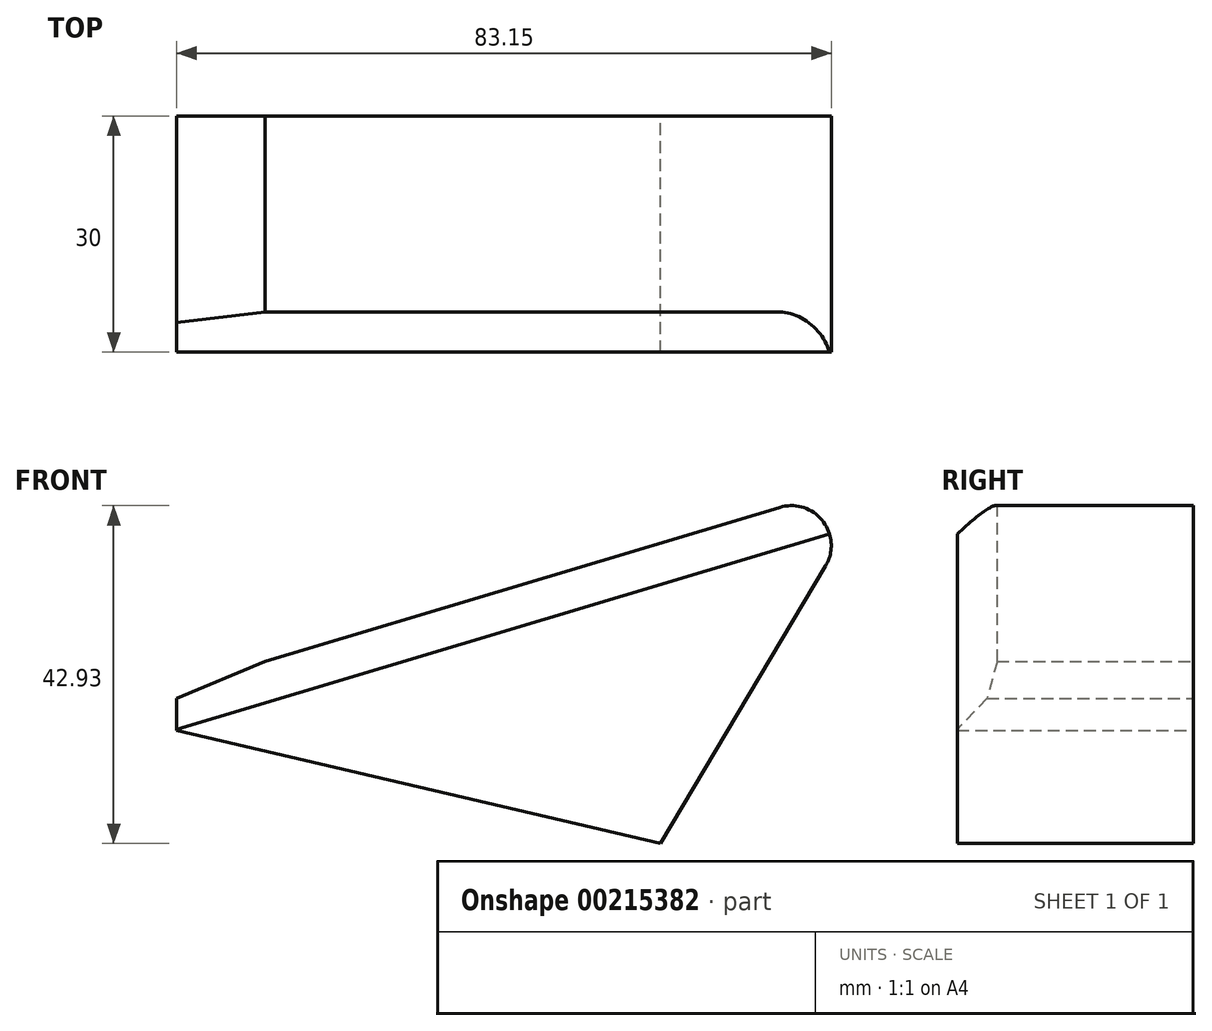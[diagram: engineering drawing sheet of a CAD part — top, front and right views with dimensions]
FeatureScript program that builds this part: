
annotation { "Feature Type Name" : "Feature", "Feature Type Description" : "" }
export const myFeature = defineFeature(function(context is Context, id is Id, definition is map)
    precondition{}
    {
        {
            var Q0;
            Q0=qCreatedBy(makeId("Front.planeOp"),FACE);
            var sketch = newSketch(context, id + "F0", { "sketchPlane" : qUnion([Q0])});
            skLineSegment(sketch, "E0", {"start": v(-72.91, 43.43) * mm, "end": v(-72.91, 47.52) * mm});
            skLineSegment(sketch, "E1", {"start": v(-61.71, 52.23) * mm, "end": v(16.19, 75.54) * mm});
            skLineSegment(sketch, "E2", {"start": v(-61.71, 52.23) * mm, "end": v(-72.91, 47.52) * mm});
            skLineSegment(sketch, "E3", {"start": v(-72.91, 43.43) * mm, "end": v(-11.47, 29.08) * mm});
            skLineSegment(sketch, "E4", {"start": v(-11.47, 29.08) * mm, "end": v(16.19, 75.54) * mm});
            skSolve(sketch);
        }
        {
            var Q0;
            Q0=makeQuery(id+"F0.imprint","IMPRINT",FACE,{"disambiguationData":[TD([[makeQuery(id+"F0.imprint","IMPRINT",EDGE,{"derivedFrom":sQuery(id+"F0.wireOp",EDGE,"E0")}),-1.0]])]});
            extrude(context, id + "F1", {"entities" : qUnion([Q0]), "depth" : 30 * mm});
        }
        {
            var Q0;
            Q0=makeQuery(id+"F1.opExtrude","CAP_EDGE",EDGE,{"disambiguationData":[OSD([sQuery(id+"F0.wireOp",EDGE,"E1")])],"isStart":false});
            chamfer(context, id + "F2", {"entities" : qUnion([Q0]), "width" : 5.08 * mm, "tangentPropagation" : true});
        }
        {
            var Q0;
            Q0=makeQuery(id+"F1.opExtrude","SWEPT_EDGE",EDGE,{"disambiguationData":[OSD([sQuery(id+"F0.wireOp",EDGE,"E1"),sQuery(id+"F0.wireOp",EDGE,"E4")])]});
            fillet(context, id + "F3", {"entities" : qUnion([Q0]), "radius" : 5.08 * mm, "tangentPropagation" : true, "allowEdgeOverflow" : false});
        }
    });
